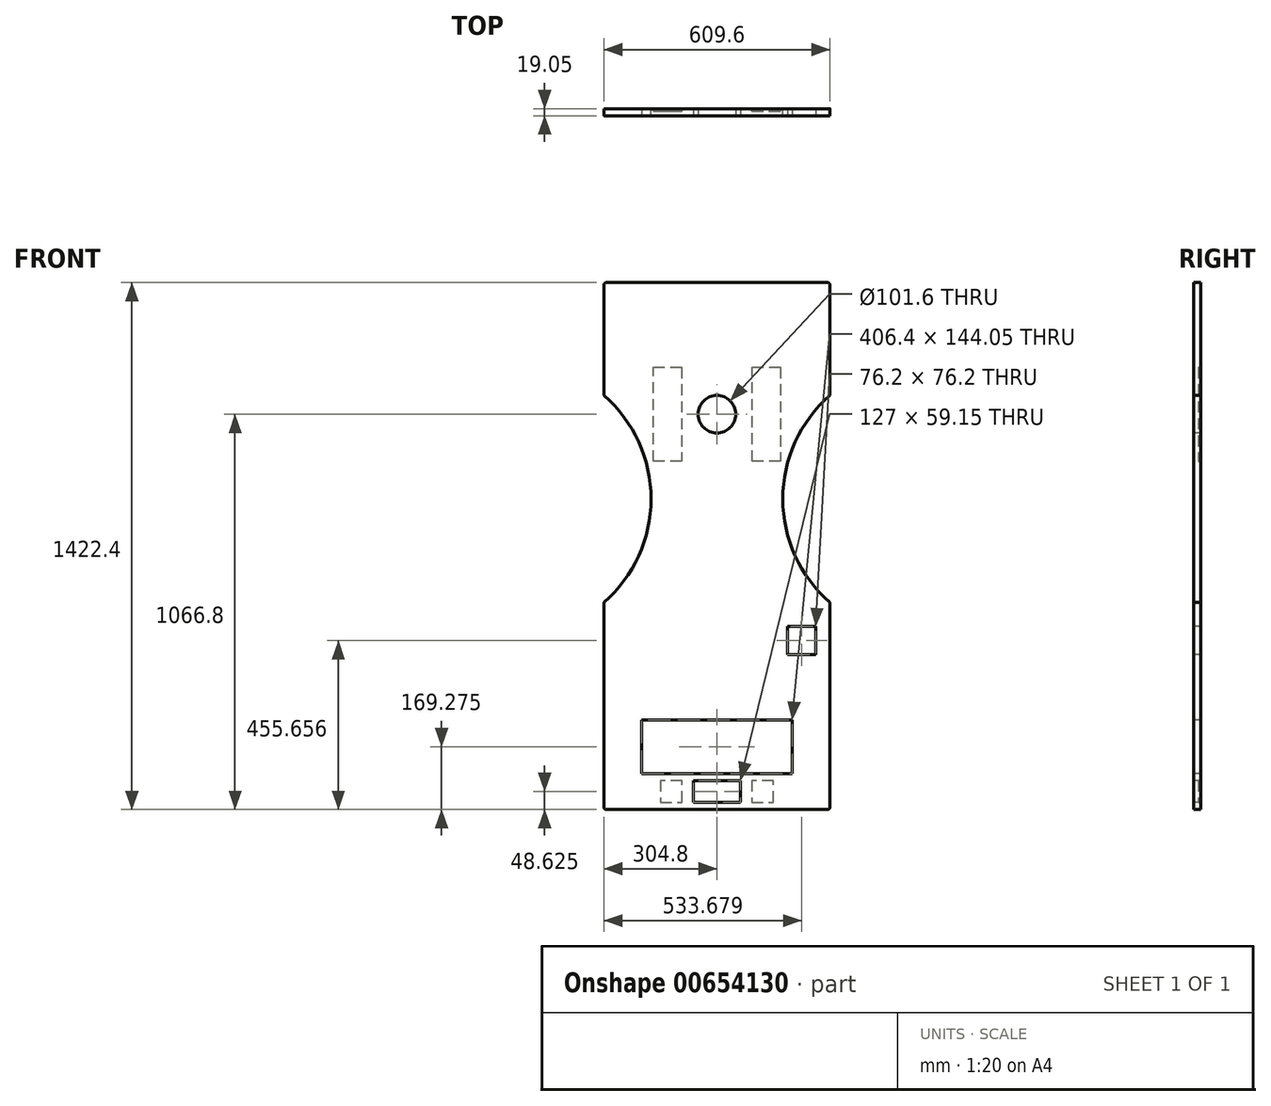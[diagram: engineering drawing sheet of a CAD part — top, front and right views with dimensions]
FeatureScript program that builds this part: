
annotation { "Feature Type Name" : "Feature", "Feature Type Description" : "" }
export const myFeature = defineFeature(function(context is Context, id is Id, definition is map)
    precondition{}
    {
        {
            var Q0;
            Q0=qCreatedBy(makeId("Front.planeOp"),FACE);
            var sketch = newSketch(context, id + "F0", { "sketchPlane" : qUnion([Q0])});
            skLineSegment(sketch, "E0.bottom", {"start": v(-298.45, 711.2) * mm, "end": v(298.45, 711.2) * mm});
            skLineSegment(sketch, "E0.top", {"start": v(-298.45, -711.2) * mm, "end": v(298.45, -711.2) * mm});
            skLineSegment(sketch, "E0.left", {"start": v(-304.8, 704.85) * mm, "end": v(-304.8, 406.4) * mm});
            skPoint(sketch, "E0.middle", {"position": v(0, 0) * mm});
            skLineSegment(sketch, "E1.trimOffspring", {"start": v(-304.8, -152.4) * mm, "end": v(-304.8, -704.85) * mm});
            skLineSegment(sketch, "E2.trimOffspring", {"start": v(304.8, -152.4) * mm, "end": v(304.8, -704.85) * mm});
            skArc(sketch, "E3", {"start": v(-304.8, -152.4) * mm, "mid": v(-177.8, 127) * mm, "end": v(-304.8, 406.4) * mm});
            skArc(sketch, "E4.MirrorCS", {"start": v(304.8, -152.4) * mm, "mid": v(177.8, 127) * mm, "end": v(304.8, 406.4) * mm});
            skPoint(sketch, "E5.visualSharp", {"position": v(-304.8, 711.2) * mm});
            skArc(sketch, "E5.filletArc", {"start": v(-298.45, 711.2) * mm, "mid": v(-302.94, 709.34) * mm, "end": v(-304.8, 704.85) * mm});
            skPoint(sketch, "E6.visualSharp", {"position": v(-304.8, -711.2) * mm});
            skArc(sketch, "E6.filletArc", {"start": v(-304.8, -704.85) * mm, "mid": v(-302.94, -709.34) * mm, "end": v(-298.45, -711.2) * mm});
            skPoint(sketch, "E7.visualSharp", {"position": v(304.8, -711.2) * mm});
            skArc(sketch, "E7.filletArc", {"start": v(298.45, -711.2) * mm, "mid": v(302.94, -709.34) * mm, "end": v(304.8, -704.85) * mm});
            skLineSegment(sketch, "E8", {"start": v(304.8, 406.4) * mm, "end": v(304.8, 704.85) * mm});
            skArc(sketch, "E9.filletArc", {"start": v(304.8, 704.85) * mm, "mid": v(302.94, 709.34) * mm, "end": v(298.45, 711.2) * mm});
            skLineSegment(sketch, "E10", {"start": v(177.8, 127) * mm, "end": v(-177.8, 127) * mm, "construction": true});
            skSolve(sketch);
        }
        {
            var Q0;
            Q0=qSketchRegion(id+"F0",true);
            extrude(context, id + "F1", {"entities" : qUnion([Q0]), "depth" : 19.05 * mm, "offsetDistance" : 25.4 * mm});
        }
        {
            var Q0;
            Q0=makeQuery(id+"F1.opExtrude","CAP_FACE",FACE,{"disambiguationData":[OSD([sQuery(id+"F0.wireOp",EDGE,"E0.bottom"),sQuery(id+"F0.wireOp",EDGE,"E0.top"),sQuery(id+"F0.wireOp",EDGE,"E0.left"),sQuery(id+"F0.wireOp",EDGE,"E0.right"),sQuery(id+"F0.wireOp",EDGE,"511ab67b-389e-4583-bde5-4cd6066dfc6e.sketch_text.stroke-37"),sQuery(id+"F0.wireOp",EDGE,"511ab67b-389e-4583-bde5-4cd6066dfc6e.sketch_text.stroke-38"),sQuery(id+"F0.wireOp",EDGE,"511ab67b-389e-4583-bde5-4cd6066dfc6e.sketch_text.stroke-39"),sQuery(id+"F0.wireOp",EDGE,"511ab67b-389e-4583-bde5-4cd6066dfc6e.sketch_text.stroke-40"),sQuery(id+"F0.wireOp",EDGE,"511ab67b-389e-4583-bde5-4cd6066dfc6e.sketch_text.stroke-41"),sQuery(id+"F0.wireOp",EDGE,"511ab67b-389e-4583-bde5-4cd6066dfc6e.sketch_text.stroke-42"),sQuery(id+"F0.wireOp",EDGE,"511ab67b-389e-4583-bde5-4cd6066dfc6e.sketch_text.stroke-44"),sQuery(id+"F0.wireOp",EDGE,"511ab67b-389e-4583-bde5-4cd6066dfc6e.sketch_text.stroke-45"),sQuery(id+"F0.wireOp",EDGE,"511ab67b-389e-4583-bde5-4cd6066dfc6e.sketch_text.stroke-46"),sQuery(id+"F0.wireOp",EDGE,"511ab67b-389e-4583-bde5-4cd6066dfc6e.sketch_text.stroke-47"),sQuery(id+"F0.wireOp",EDGE,"511ab67b-389e-4583-bde5-4cd6066dfc6e.sketch_text.stroke-48"),sQuery(id+"F0.wireOp",EDGE,"511ab67b-389e-4583-bde5-4cd6066dfc6e.sketch_text.stroke-49"),sQuery(id+"F0.wireOp",EDGE,"511ab67b-389e-4583-bde5-4cd6066dfc6e.sketch_text.stroke-50"),sQuery(id+"F0.wireOp",EDGE,"511ab67b-389e-4583-bde5-4cd6066dfc6e.sketch_text.stroke-51"),sQuery(id+"F0.wireOp",EDGE,"511ab67b-389e-4583-bde5-4cd6066dfc6e.sketch_text.stroke-52"),sQuery(id+"F0.wireOp",EDGE,"511ab67b-389e-4583-bde5-4cd6066dfc6e.sketch_text.stroke-53"),sQuery(id+"F0.wireOp",EDGE,"511ab67b-389e-4583-bde5-4cd6066dfc6e.sketch_text.stroke-54"),sQuery(id+"F0.wireOp",EDGE,"511ab67b-389e-4583-bde5-4cd6066dfc6e.sketch_text.stroke-55"),sQuery(id+"F0.wireOp",EDGE,"511ab67b-389e-4583-bde5-4cd6066dfc6e.sketch_text.stroke-56"),sQuery(id+"F0.wireOp",EDGE,"511ab67b-389e-4583-bde5-4cd6066dfc6e.sketch_text.stroke-57"),sQuery(id+"F0.wireOp",EDGE,"511ab67b-389e-4583-bde5-4cd6066dfc6e.sketch_text.stroke-58"),sQuery(id+"F0.wireOp",EDGE,"511ab67b-389e-4583-bde5-4cd6066dfc6e.sketch_text.stroke-59"),sQuery(id+"F0.wireOp",EDGE,"511ab67b-389e-4583-bde5-4cd6066dfc6e.sketch_text.stroke-60"),sQuery(id+"F0.wireOp",EDGE,"511ab67b-389e-4583-bde5-4cd6066dfc6e.sketch_text.stroke-61"),sQuery(id+"F0.wireOp",EDGE,"511ab67b-389e-4583-bde5-4cd6066dfc6e.sketch_text.stroke-62"),sQuery(id+"F0.wireOp",EDGE,"511ab67b-389e-4583-bde5-4cd6066dfc6e.sketch_text.stroke-63"),sQuery(id+"F0.wireOp",EDGE,"511ab67b-389e-4583-bde5-4cd6066dfc6e.sketch_text.stroke-64"),sQuery(id+"F0.wireOp",EDGE,"511ab67b-389e-4583-bde5-4cd6066dfc6e.sketch_text.stroke-65"),sQuery(id+"F0.wireOp",EDGE,"511ab67b-389e-4583-bde5-4cd6066dfc6e.sketch_text.stroke-66"),sQuery(id+"F0.wireOp",EDGE,"511ab67b-389e-4583-bde5-4cd6066dfc6e.sketch_text.stroke-67"),sQuery(id+"F0.wireOp",EDGE,"511ab67b-389e-4583-bde5-4cd6066dfc6e.sketch_text.stroke-68"),sQuery(id+"F0.wireOp",EDGE,"511ab67b-389e-4583-bde5-4cd6066dfc6e.sketch_text.stroke-69"),sQuery(id+"F0.wireOp",EDGE,"511ab67b-389e-4583-bde5-4cd6066dfc6e.sketch_text.stroke-70"),sQuery(id+"F0.wireOp",EDGE,"511ab67b-389e-4583-bde5-4cd6066dfc6e.sketch_text.stroke-71"),sQuery(id+"F0.wireOp",EDGE,"511ab67b-389e-4583-bde5-4cd6066dfc6e.sketch_text.stroke-72"),sQuery(id+"F0.wireOp",EDGE,"511ab67b-389e-4583-bde5-4cd6066dfc6e.sketch_text.stroke-73"),sQuery(id+"F0.wireOp",EDGE,"511ab67b-389e-4583-bde5-4cd6066dfc6e.sketch_text.stroke-74"),sQuery(id+"F0.wireOp",EDGE,"511ab67b-389e-4583-bde5-4cd6066dfc6e.sketch_text.stroke-75"),sQuery(id+"F0.wireOp",EDGE,"511ab67b-389e-4583-bde5-4cd6066dfc6e.sketch_text.stroke-76"),sQuery(id+"F0.wireOp",EDGE,"511ab67b-389e-4583-bde5-4cd6066dfc6e.sketch_text.stroke-77"),sQuery(id+"F0.wireOp",EDGE,"511ab67b-389e-4583-bde5-4cd6066dfc6e.sketch_text.stroke-78"),sQuery(id+"F0.wireOp",EDGE,"511ab67b-389e-4583-bde5-4cd6066dfc6e.sketch_text.stroke-79"),sQuery(id+"F0.wireOp",EDGE,"511ab67b-389e-4583-bde5-4cd6066dfc6e.sketch_text.stroke-80"),sQuery(id+"F0.wireOp",EDGE,"511ab67b-389e-4583-bde5-4cd6066dfc6e.sketch_text.stroke-81"),sQuery(id+"F0.wireOp",EDGE,"511ab67b-389e-4583-bde5-4cd6066dfc6e.sketch_text.stroke-82"),sQuery(id+"F0.wireOp",EDGE,"511ab67b-389e-4583-bde5-4cd6066dfc6e.sketch_text.stroke-83"),sQuery(id+"F0.wireOp",EDGE,"511ab67b-389e-4583-bde5-4cd6066dfc6e.sketch_text.stroke-84"),sQuery(id+"F0.wireOp",EDGE,"511ab67b-389e-4583-bde5-4cd6066dfc6e.sketch_text.stroke-85"),sQuery(id+"F0.wireOp",EDGE,"511ab67b-389e-4583-bde5-4cd6066dfc6e.sketch_text.stroke-86"),sQuery(id+"F0.wireOp",EDGE,"511ab67b-389e-4583-bde5-4cd6066dfc6e.sketch_text.stroke-87"),sQuery(id+"F0.wireOp",EDGE,"511ab67b-389e-4583-bde5-4cd6066dfc6e.sketch_text.stroke-88"),sQuery(id+"F0.wireOp",EDGE,"511ab67b-389e-4583-bde5-4cd6066dfc6e.sketch_text.stroke-90"),sQuery(id+"F0.wireOp",EDGE,"511ab67b-389e-4583-bde5-4cd6066dfc6e.sketch_text.stroke-91"),sQuery(id+"F0.wireOp",EDGE,"511ab67b-389e-4583-bde5-4cd6066dfc6e.sketch_text.stroke-92"),sQuery(id+"F0.wireOp",EDGE,"511ab67b-389e-4583-bde5-4cd6066dfc6e.sketch_text.stroke-93"),sQuery(id+"F0.wireOp",EDGE,"511ab67b-389e-4583-bde5-4cd6066dfc6e.sketch_text.stroke-94"),sQuery(id+"F0.wireOp",EDGE,"511ab67b-389e-4583-bde5-4cd6066dfc6e.sketch_text.stroke-95"),sQuery(id+"F0.wireOp",EDGE,"511ab67b-389e-4583-bde5-4cd6066dfc6e.sketch_text.stroke-97"),sQuery(id+"F0.wireOp",EDGE,"511ab67b-389e-4583-bde5-4cd6066dfc6e.sketch_text.stroke-98"),sQuery(id+"F0.wireOp",EDGE,"511ab67b-389e-4583-bde5-4cd6066dfc6e.sketch_text.stroke-99"),sQuery(id+"F0.wireOp",EDGE,"511ab67b-389e-4583-bde5-4cd6066dfc6e.sketch_text.stroke-100"),sQuery(id+"F0.wireOp",EDGE,"511ab67b-389e-4583-bde5-4cd6066dfc6e.sketch_text.stroke-101"),sQuery(id+"F0.wireOp",EDGE,"511ab67b-389e-4583-bde5-4cd6066dfc6e.sketch_text.stroke-102"),sQuery(id+"F0.wireOp",EDGE,"511ab67b-389e-4583-bde5-4cd6066dfc6e.sketch_text.stroke-103"),sQuery(id+"F0.wireOp",EDGE,"511ab67b-389e-4583-bde5-4cd6066dfc6e.sketch_text.stroke-104"),sQuery(id+"F0.wireOp",EDGE,"511ab67b-389e-4583-bde5-4cd6066dfc6e.sketch_text.stroke-105"),sQuery(id+"F0.wireOp",EDGE,"511ab67b-389e-4583-bde5-4cd6066dfc6e.sketch_text.stroke-106"),sQuery(id+"F0.wireOp",EDGE,"511ab67b-389e-4583-bde5-4cd6066dfc6e.sketch_text.stroke-107"),sQuery(id+"F0.wireOp",EDGE,"511ab67b-389e-4583-bde5-4cd6066dfc6e.sketch_text.stroke-108"),sQuery(id+"F0.wireOp",EDGE,"511ab67b-389e-4583-bde5-4cd6066dfc6e.sketch_text.stroke-109"),sQuery(id+"F0.wireOp",EDGE,"511ab67b-389e-4583-bde5-4cd6066dfc6e.sketch_text.stroke-110")])],"isStart":false});
            var sketch = newSketch(context, id + "F2", { "sketchPlane" : qUnion([Q0])});
            skCircle(sketch, "E11", {"center": v(0, 355.6) * mm, "radius": 50.8 * mm});
            skLineSegment(sketch, "E12", {"start": v(-203.2, -469.9) * mm, "end": v(203.2, -469.9) * mm});
            skLineSegment(sketch, "E13", {"start": v(203.2, -469.9) * mm, "end": v(203.2, -613.95) * mm});
            skLineSegment(sketch, "E14", {"start": v(203.2, -613.95) * mm, "end": v(-203.2, -613.95) * mm});
            skLineSegment(sketch, "E15", {"start": v(-203.2, -613.95) * mm, "end": v(-203.2, -469.9) * mm});
            skLineSegment(sketch, "E16", {"start": v(190.78, -293.64) * mm, "end": v(266.98, -293.64) * mm});
            skLineSegment(sketch, "E17", {"start": v(266.98, -293.64) * mm, "end": v(266.98, -217.44) * mm});
            skLineSegment(sketch, "E18", {"start": v(266.98, -217.44) * mm, "end": v(190.78, -217.44) * mm});
            skLineSegment(sketch, "E19", {"start": v(190.78, -217.44) * mm, "end": v(190.78, -293.64) * mm});
            skLineSegment(sketch, "E20", {"start": v(63.5, -633) * mm, "end": v(63.5, -692.15) * mm});
            skLineSegment(sketch, "E21", {"start": v(63.5, -692.15) * mm, "end": v(-63.5, -692.15) * mm});
            skLineSegment(sketch, "E22", {"start": v(-63.5, -692.15) * mm, "end": v(-63.5, -633) * mm});
            skLineSegment(sketch, "E23", {"start": v(-63.5, -633) * mm, "end": v(63.5, -633) * mm});
            skSolve(sketch);
        }
        {
            var Q0;
            Q0=makeQuery(id+"F2.imprint","IMPRINT",FACE,{"disambiguationData":[TD([[makeQuery(id+"F2.imprint","IMPRINT",EDGE,{"derivedFrom":sQuery(id+"F2.wireOp",EDGE,"E11")}),1.0]])]});
            var Q1;
            Q1=makeQuery(id+"F2.imprint","IMPRINT",FACE,{"disambiguationData":[TD([[makeQuery(id+"F2.imprint","IMPRINT",EDGE,{"derivedFrom":sQuery(id+"F2.wireOp",EDGE,"E16")}),1.0]])]});
            var Q2;
            Q2=makeQuery(id+"F2.imprint","IMPRINT",FACE,{"disambiguationData":[TD([[makeQuery(id+"F2.imprint","IMPRINT",EDGE,{"derivedFrom":sQuery(id+"F2.wireOp",EDGE,"E12")}),-1.0]])]});
            extrude(context, id + "F3", {"entities" : qUnion([Q0, Q1, Q2]), "operationType" : NewBodyOperationType.REMOVE, "endBound" : BoundingType.THROUGH_ALL, "oppositeDirection" : true, "depth" : 12.7 * mm, "offsetDistance" : 25.4 * mm});
        }
        {
            var Q0;
            Q0=makeQuery(id+"F0.imprint","IMPRINT",FACE,{"disambiguationData":[TD([[makeQuery(id+"F0.imprint","IMPRINT",EDGE,{"derivedFrom":sQuery(id+"F0.wireOp",EDGE,"E0.bottom")}),-1.0]])]});
            var sketch = newSketch(context, id + "F4", { "sketchPlane" : qUnion([Q0])});
            skLineSegment(sketch, "E24", {"start": v(93.98, -691.42) * mm, "end": v(152.4, -691.42) * mm});
            skLineSegment(sketch, "E25", {"start": v(152.4, -691.42) * mm, "end": v(152.4, -633) * mm});
            skLineSegment(sketch, "E26", {"start": v(152.4, -633) * mm, "end": v(93.98, -633) * mm});
            skLineSegment(sketch, "E27", {"start": v(93.98, -633) * mm, "end": v(93.98, -691.42) * mm});
            skLineSegment(sketch, "E28", {"start": v(-152.4, -691.42) * mm, "end": v(-93.98, -691.42) * mm});
            skLineSegment(sketch, "E29", {"start": v(-93.98, -691.42) * mm, "end": v(-93.98, -633) * mm});
            skLineSegment(sketch, "E30", {"start": v(-93.98, -633) * mm, "end": v(-152.4, -633) * mm});
            skLineSegment(sketch, "E31", {"start": v(-152.4, -633) * mm, "end": v(-152.4, -691.42) * mm});
            skLineSegment(sketch, "E32", {"start": v(95.25, 482.6) * mm, "end": v(171.45, 482.6) * mm});
            skLineSegment(sketch, "E33", {"start": v(171.45, 482.6) * mm, "end": v(171.45, 228.6) * mm});
            skLineSegment(sketch, "E34", {"start": v(171.45, 228.6) * mm, "end": v(95.25, 228.6) * mm});
            skLineSegment(sketch, "E35", {"start": v(95.25, 228.6) * mm, "end": v(95.25, 482.6) * mm});
            skLineSegment(sketch, "E36", {"start": v(-95.25, 482.6) * mm, "end": v(-95.25, 228.6) * mm});
            skLineSegment(sketch, "E37", {"start": v(-95.25, 228.6) * mm, "end": v(-171.45, 228.6) * mm});
            skLineSegment(sketch, "E38", {"start": v(-171.45, 228.6) * mm, "end": v(-171.45, 482.6) * mm});
            skLineSegment(sketch, "E39", {"start": v(-171.45, 482.6) * mm, "end": v(-95.25, 482.6) * mm});
            skLineSegment(sketch, "E40", {"start": v(190.84, -293.8) * mm, "end": v(190.84, -710.39) * mm});
            skSolve(sketch);
        }
        {
            var Q0;
            Q0=makeQuery(id+"F4.imprint","IMPRINT",FACE,{"disambiguationData":[TD([[makeQuery(id+"F4.imprint","IMPRINT",EDGE,{"derivedFrom":sQuery(id+"F4.wireOp",EDGE,"E24")}),1.0]])]});
            var Q1;
            Q1=makeQuery(id+"F4.imprint","IMPRINT",FACE,{"disambiguationData":[TD([[makeQuery(id+"F4.imprint","IMPRINT",EDGE,{"derivedFrom":sQuery(id+"F4.wireOp",EDGE,"E28")}),1.0]])]});
            var Q2;
            Q2=makeQuery(id+"F4.imprint","IMPRINT",FACE,{"disambiguationData":[TD([[makeQuery(id+"F4.imprint","IMPRINT",EDGE,{"derivedFrom":sQuery(id+"F4.wireOp",EDGE,"E32")}),-1.0]])]});
            var Q3;
            Q3=makeQuery(id+"F4.imprint","IMPRINT",FACE,{"disambiguationData":[TD([[makeQuery(id+"F4.imprint","IMPRINT",EDGE,{"derivedFrom":sQuery(id+"F4.wireOp",EDGE,"E36")}),-1.0]])]});
            extrude(context, id + "F5", {"entities" : qUnion([Q0, Q1, Q2, Q3]), "operationType" : NewBodyOperationType.REMOVE, "depth" : 6.35 * mm, "offsetDistance" : 25.4 * mm});
        }
        {
            var Q0;
            Q0=makeQuery(id+"F2.imprint","IMPRINT",FACE,{"disambiguationData":[TD([[makeQuery(id+"F2.imprint","IMPRINT",EDGE,{"derivedFrom":sQuery(id+"F2.wireOp",EDGE,"E20")}),-1.0]])]});
            extrude(context, id + "F6", {"entities" : qUnion([Q0]), "operationType" : NewBodyOperationType.REMOVE, "endBound" : BoundingType.THROUGH_ALL, "oppositeDirection" : true, "depth" : 25.4 * mm, "offsetDistance" : 25.4 * mm});
        }
    });
